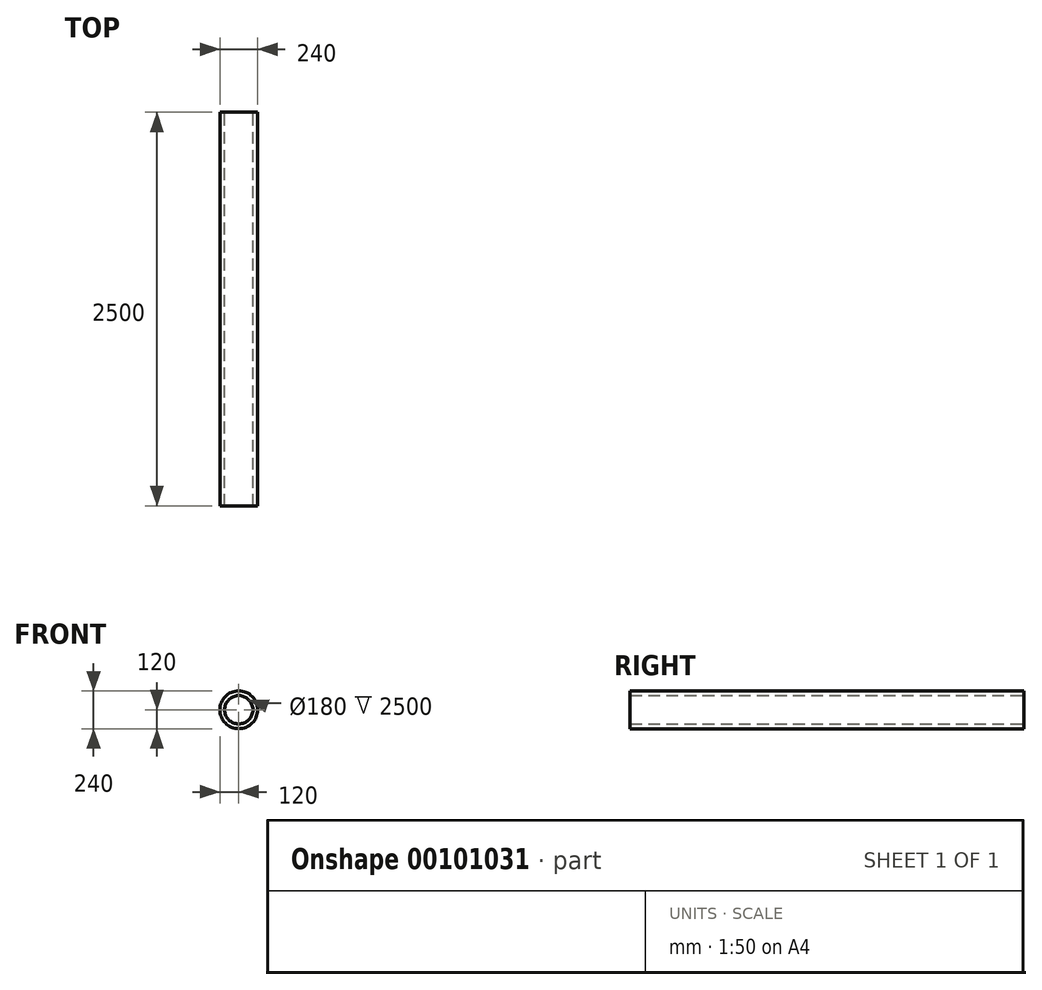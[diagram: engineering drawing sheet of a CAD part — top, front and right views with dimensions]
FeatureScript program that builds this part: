
annotation { "Feature Type Name" : "Feature", "Feature Type Description" : "" }
export const myFeature = defineFeature(function(context is Context, id is Id, definition is map)
    precondition{}
    {
        {
            var Q0;
            Q0=qCreatedBy(makeId("Front.planeOp"),FACE);
            var sketch = newSketch(context, id + "F0", { "sketchPlane" : qUnion([Q0])});
            skCircle(sketch, "E0", {"center": v(0, 0) * mm, "radius": 90 * mm});
            skCircle(sketch, "E1", {"center": v(0, 0) * mm, "radius": 120 * mm});
            skSolve(sketch);
        }
        {
            var Q0;
            Q0=makeQuery(id+"F0.imprint","IMPRINT",FACE,{"disambiguationData":[TD([[makeQuery(id+"F0.imprint","IMPRINT",EDGE,{"derivedFrom":sQuery(id+"F0.wireOp",EDGE,"E0")}),-1.0]])]});
            extrude(context, id + "F1", {"entities" : qUnion([Q0]), "depth" : 2500 * mm});
        }
    });
